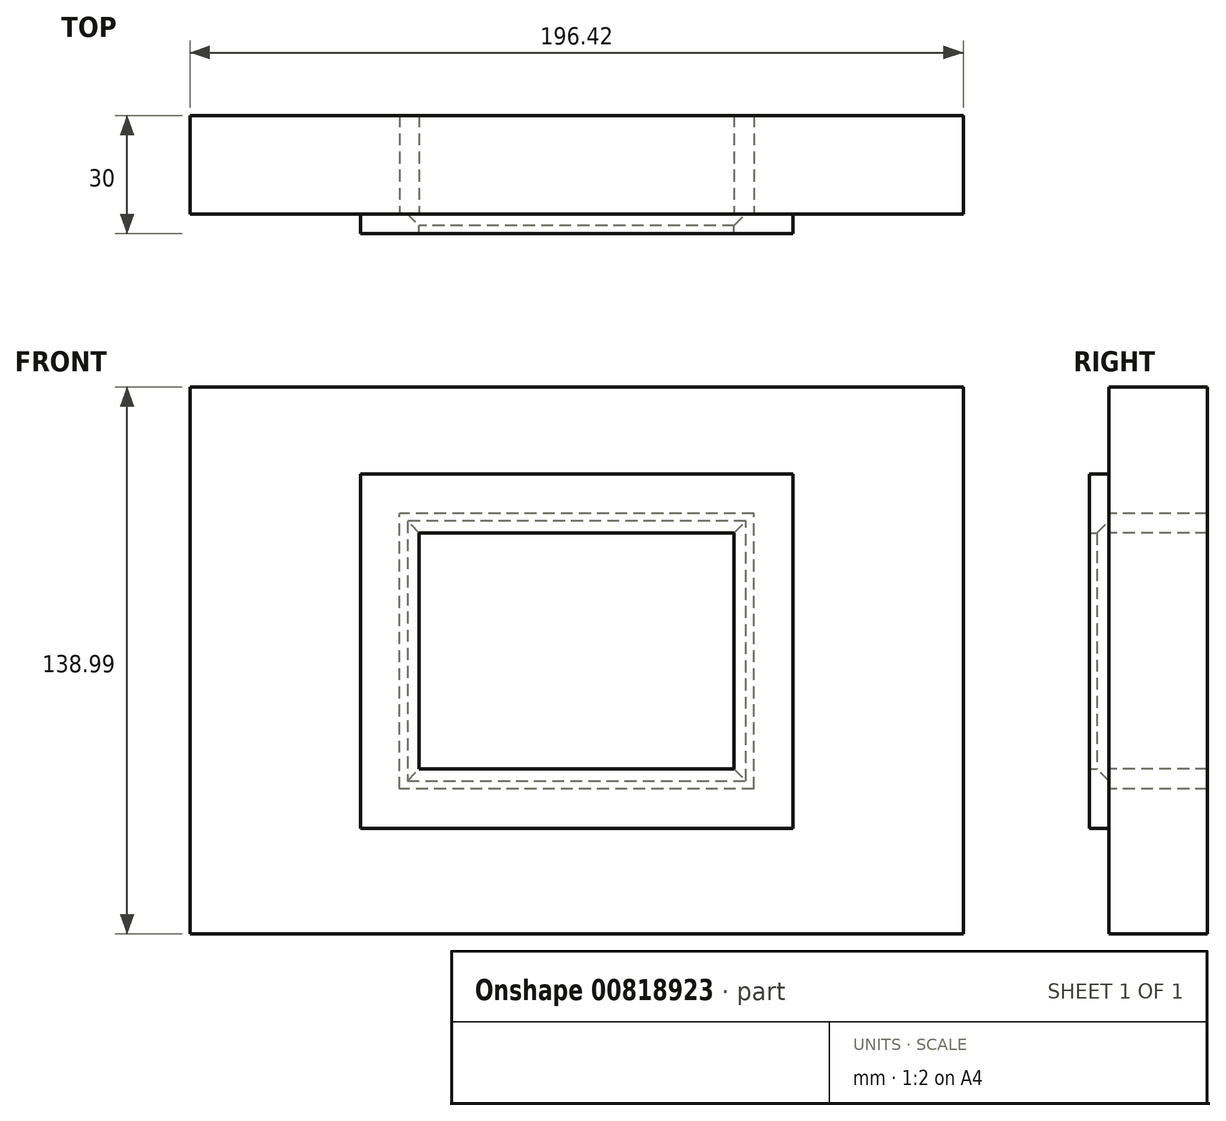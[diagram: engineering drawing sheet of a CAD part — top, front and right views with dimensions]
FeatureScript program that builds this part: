
annotation { "Feature Type Name" : "Feature", "Feature Type Description" : "" }
export const myFeature = defineFeature(function(context is Context, id is Id, definition is map)
    precondition{}
    {
        {
            var Q0;
            Q0=qCreatedBy(makeId("Front.planeOp"),FACE);
            var sketch = newSketch(context, id + "F0", { "sketchPlane" : qUnion([Q0])});
            skLineSegment(sketch, "E0.bottom", {"start": v(40, -30) * mm, "end": v(-40, -30) * mm});
            skLineSegment(sketch, "E0.top", {"start": v(40, 30) * mm, "end": v(-40, 30) * mm});
            skLineSegment(sketch, "E0.left", {"start": v(40, -30) * mm, "end": v(40, 30) * mm});
            skLineSegment(sketch, "E0.right", {"start": v(-40, -30) * mm, "end": v(-40, 30) * mm});
            skPoint(sketch, "E0.middle", {"position": v(0, 0) * mm});
            skSolve(sketch);
        }
        {
            var Q0;
            Q0=makeQuery(id+"F0.imprint","IMPRINT",FACE,{"disambiguationData":[TD([[makeQuery(id+"F0.imprint","IMPRINT",EDGE,{"derivedFrom":sQuery(id+"F0.wireOp",EDGE,"E0.bottom")}),-1.0]])]});
            extrude(context, id + "F1", {"entities" : qUnion([Q0]), "oppositeDirection" : true, "depth" : 25 * mm, "offsetDistance" : 25 * mm});
        }
        {
            var Q0;
            Q0=makeQuery(id+"F1.opExtrude","CAP_FACE",FACE,{"disambiguationData":[OSD([sQuery(id+"F0.wireOp",EDGE,"E0.bottom"),sQuery(id+"F0.wireOp",EDGE,"E0.top"),sQuery(id+"F0.wireOp",EDGE,"E0.left"),sQuery(id+"F0.wireOp",EDGE,"E0.right")])],"isStart":true});
            var sketch = newSketch(context, id + "F2", { "sketchPlane" : qUnion([Q0])});
            skLineSegment(sketch, "E1.bottom", {"start": v(45, -35) * mm, "end": v(-45, -35) * mm});
            skLineSegment(sketch, "E1.top", {"start": v(45, 35) * mm, "end": v(-45, 35) * mm});
            skLineSegment(sketch, "E1.left", {"start": v(45, -35) * mm, "end": v(45, 35) * mm});
            skLineSegment(sketch, "E1.right", {"start": v(-45, -35) * mm, "end": v(-45, 35) * mm});
            skPoint(sketch, "E1.middle", {"position": v(0, 0) * mm});
            skLineSegment(sketch, "E2.bottom", {"start": v(98.21, -71.91) * mm, "end": v(-98.21, -71.91) * mm});
            skLineSegment(sketch, "E2.top", {"start": v(98.21, 67.08) * mm, "end": v(-98.21, 67.08) * mm});
            skLineSegment(sketch, "E2.left", {"start": v(98.21, -71.91) * mm, "end": v(98.21, 67.08) * mm});
            skLineSegment(sketch, "E2.right", {"start": v(-98.21, -71.91) * mm, "end": v(-98.21, 67.08) * mm});
            skPoint(sketch, "E2.middle", {"position": v(0, -2.41) * mm});
            skSolve(sketch);
        }
        {
            var Q0;
            Q0=makeQuery(id+"F2.imprint","IMPRINT",FACE,{"disambiguationData":[TD([[makeQuery(id+"F2.imprint","IMPRINT",EDGE,{"derivedFrom":sQuery(id+"F2.wireOp",EDGE,"E1.bottom")}),1.0]])]});
            extrude(context, id + "F3", {"entities" : qUnion([Q0]), "oppositeDirection" : true, "depth" : 25 * mm, "offsetDistance" : 25 * mm});
        }
        {
            var Q0;
            Q0=makeQuery(id+"F3.opExtrude","CAP_FACE",FACE,{"disambiguationData":[OSD([sQuery(id+"F2.wireOp",EDGE,"E1.bottom"),sQuery(id+"F2.wireOp",EDGE,"E1.top"),sQuery(id+"F2.wireOp",EDGE,"E1.left"),sQuery(id+"F2.wireOp",EDGE,"E1.right"),sQuery(id+"F2.wireOp",EDGE,"E2.bottom"),sQuery(id+"F2.wireOp",EDGE,"E2.top"),sQuery(id+"F2.wireOp",EDGE,"E2.left"),sQuery(id+"F2.wireOp",EDGE,"E2.right")])],"isStart":true});
            var sketch = newSketch(context, id + "F4", { "sketchPlane" : qUnion([Q0])});
            skLineSegment(sketch, "E3.bottom", {"start": v(40, -30) * mm, "end": v(-40, -30) * mm});
            skLineSegment(sketch, "E3.top", {"start": v(40, 30) * mm, "end": v(-40, 30) * mm});
            skLineSegment(sketch, "E3.left", {"start": v(40, -30) * mm, "end": v(40, 30) * mm});
            skLineSegment(sketch, "E3.right", {"start": v(-40, -30) * mm, "end": v(-40, 30) * mm});
            skPoint(sketch, "E3.middle", {"position": v(0, 0) * mm});
            skLineSegment(sketch, "E4.bottom", {"start": v(54.94, -45) * mm, "end": v(-54.94, -45) * mm});
            skLineSegment(sketch, "E4.top", {"start": v(54.94, 45) * mm, "end": v(-54.94, 45) * mm});
            skLineSegment(sketch, "E4.left", {"start": v(54.94, -45) * mm, "end": v(54.94, 45) * mm});
            skLineSegment(sketch, "E4.right", {"start": v(-54.94, -45) * mm, "end": v(-54.94, 45) * mm});
            skSolve(sketch);
        }
        {
            var Q0;
            Q0 = qSketchRegion(id + "F4", true);
            extrude(context, id + "F5", {"entities" : qUnion([Q0]), "operationType" : NewBodyOperationType.ADD, "depth" : 5 * mm, "offsetDistance" : 25 * mm});
        }
        {
            var Q0;
            Q0=makeQuery(id+"F5.opExtrude","CAP_EDGE",EDGE,{"disambiguationData":[OSD([sQuery(id+"F4.wireOp",EDGE,"E3.top")])],"isStart":true});
            var Q1;
            Q1=makeQuery(id+"F5.opExtrude","CAP_EDGE",EDGE,{"disambiguationData":[OSD([sQuery(id+"F4.wireOp",EDGE,"E3.right")])],"isStart":true});
            var Q2;
            Q2=makeQuery(id+"F5.opExtrude","CAP_EDGE",EDGE,{"disambiguationData":[OSD([sQuery(id+"F4.wireOp",EDGE,"E3.left")])],"isStart":true});
            var Q3;
            Q3=makeQuery(id+"F5.opExtrude","CAP_EDGE",EDGE,{"disambiguationData":[OSD([sQuery(id+"F4.wireOp",EDGE,"E3.bottom")])],"isStart":true});
            chamfer(context, id + "F6", {"entities" : qUnion([Q0, Q1, Q2, Q3]), "width" : 3 * mm, "tangentPropagation" : true});
        }
    });
